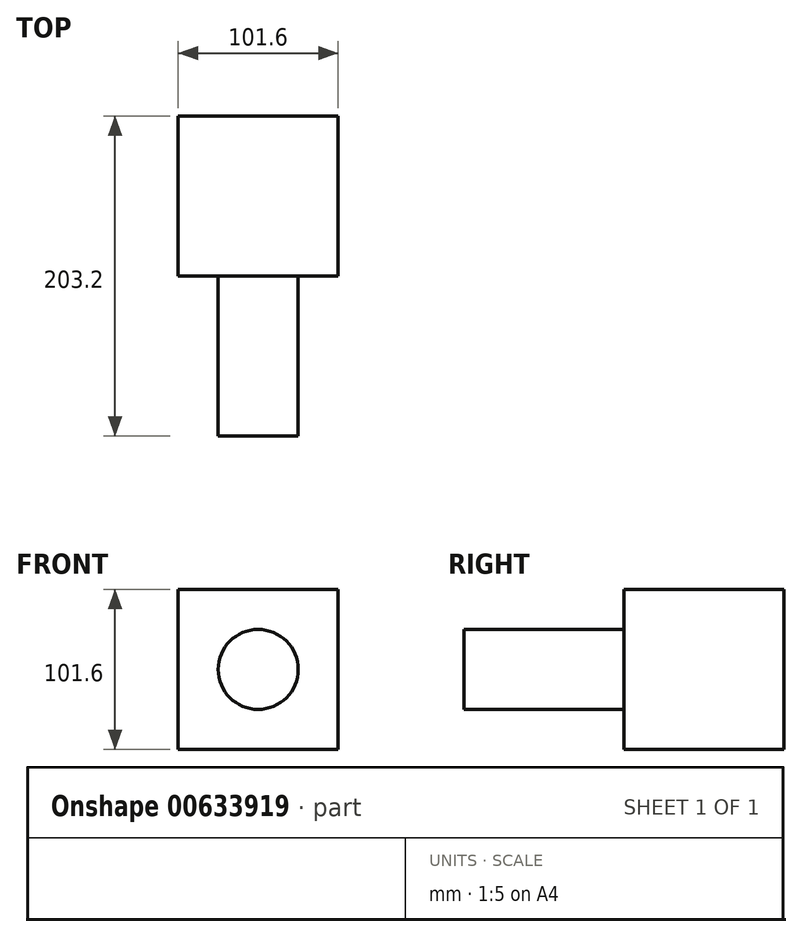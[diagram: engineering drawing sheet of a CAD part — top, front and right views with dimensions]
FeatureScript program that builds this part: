
annotation { "Feature Type Name" : "Feature", "Feature Type Description" : "" }
export const myFeature = defineFeature(function(context is Context, id is Id, definition is map)
    precondition{}
    {
        {
            var Q0;
            Q0=qCreatedBy(makeId("Front.planeOp"),FACE);
            var sketch = newSketch(context, id + "F0", { "sketchPlane" : qUnion([Q0])});
            skLineSegment(sketch, "E0.bottom", {"start": v(-52.02, 118.08) * mm, "end": v(49.58, 118.08) * mm});
            skLineSegment(sketch, "E0.top", {"start": v(-52.02, 16.48) * mm, "end": v(49.58, 16.48) * mm});
            skLineSegment(sketch, "E0.left", {"start": v(-52.02, 118.08) * mm, "end": v(-52.02, 16.48) * mm});
            skLineSegment(sketch, "E0.right", {"start": v(49.58, 118.08) * mm, "end": v(49.58, 16.48) * mm});
            skSolve(sketch);
        }
        {
            var Q0;
            Q0=makeQuery(id+"F0.imprint","IMPRINT",FACE,{"disambiguationData":[TD([[makeQuery(id+"F0.imprint","IMPRINT",EDGE,{"derivedFrom":sQuery(id+"F0.wireOp",EDGE,"E0.bottom")}),-1.0]])]});
            extrude(context, id + "F1", {"entities" : qUnion([Q0]), "oppositeDirection" : true, "depth" : 101.6 * mm, "offsetDistance" : 25.4 * mm});
        }
        {
            var Q0;
            Q0=makeQuery(id+"F1.opExtrude","CAP_FACE",FACE,{"disambiguationData":[OSD([sQuery(id+"F0.wireOp",EDGE,"E0.bottom"),sQuery(id+"F0.wireOp",EDGE,"E0.top"),sQuery(id+"F0.wireOp",EDGE,"E0.left"),sQuery(id+"F0.wireOp",EDGE,"E0.right")])],"isStart":true});
            var sketch = newSketch(context, id + "F2", { "sketchPlane" : qUnion([Q0])});
            skCircle(sketch, "E1", {"center": v(-1.22, 67.28) * mm, "radius": 25.4 * mm});
            skPoint(sketch, "E1.centerSnap0", {"position": v(49.58, 67.28) * mm});
            skPoint(sketch, "E1.centerSnap1", {"position": v(-1.22, 118.08) * mm});
            skSolve(sketch);
        }
        {
            var Q0;
            Q0=makeQuery(id+"F2.imprint","IMPRINT",FACE,{"disambiguationData":[TD([[makeQuery(id+"F2.imprint","IMPRINT",EDGE,{"derivedFrom":sQuery(id+"F2.wireOp",EDGE,"E1")}),1.0]])]});
            extrude(context, id + "F3", {"entities" : qUnion([Q0]), "operationType" : NewBodyOperationType.ADD, "depth" : 101.6 * mm, "offsetDistance" : 25.4 * mm});
        }
    });
